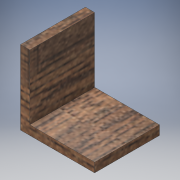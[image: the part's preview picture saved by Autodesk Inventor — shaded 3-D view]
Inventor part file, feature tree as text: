
AUTODESK INVENTOR PART (.ipt)
format: ipt  version: 2017 (Build 210142000, 142)  size: 129,024 bytes
history: native  units: in
note: dims shown in document units (in); Inventor stores cm internally (conversion verified against a paired STEP export)
features: extrude x2, sketch x2
ambient origin geometry x8: Origin, YZ Plane, XZ Plane, XY Plane, X Axis, Y Axis, Z Axis, Center Point
bodies: Solid1 (feature_tree)
feature tree (4):
  extrude  "Extrusion1"  Depth=4.0in
  extrude  "Extrusion2"  Depth=0.5in
  sketch  "Sketch1"  dims[d0=3.5in d1=4.0in]
  sketch  "Sketch2"  dims[d2=0.5in d3=0.0in d4=0.5in d5=3.5in d6=0.0in]
